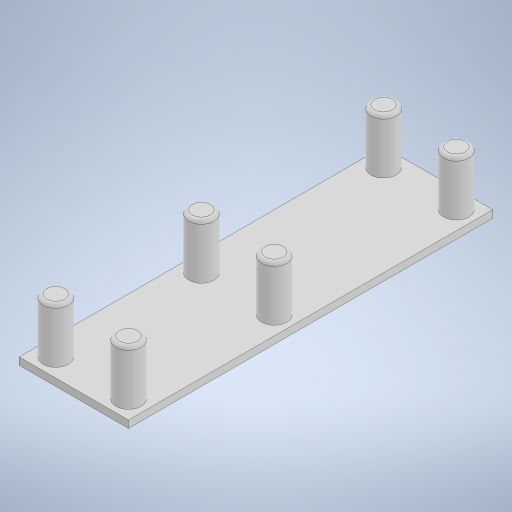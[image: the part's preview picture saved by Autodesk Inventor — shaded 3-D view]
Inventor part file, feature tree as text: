
AUTODESK INVENTOR PART (.ipt)
format: ipt  version: 2024.1 (Build 281209000, 209)  size: 441,344 bytes
history: native  units: in
note: dims shown in document units (in); Inventor stores cm internally (conversion verified against a paired STEP export)
features: extrude x4, sketch x4, fillet x2
ambient origin geometry x8: Origin, YZ Plane, XZ Plane, XY Plane, X Axis, Y Axis, Z Axis, Center Point
bodies: Solid1 (feature_tree)
feature tree (10):
  extrude  "Extrusion1"  Depth=1.1811in
  extrude  "Extrusion2"  Depth=0.0787in
  extrude  "Extrusion3"  Depth=1.5748in
  extrude  "Extrusion4"  Depth=1.969in
  fillet  "Fillet1"  Radius=1.969in
  fillet  "Fillet2"  Radius=0.3935in
  sketch  "Sketch1"  dims[d0=3.937in d1=1.1811in]
  sketch  "Sketch2"  dims[d2=0.0787in d3=0.0in d4=0.1969in]
  sketch  "Sketch3"  dims[d5=0.1969in d6=1.5748in]
  sketch  "Sketch4"  dims[d7=1.5748in d8=1.969in d9=1.969in d10=0.3935in d11=0.3935in d12=0.2756in d13=0.2756in d14=0.2756in d15=0.2756in d16=0.2756in d17=0.2756in d18=0.2362in d19=0.2362in d20=0.2362in d21=0.2362in d22=0.2362in d23=0.2362in d24=0.5512in d25=0.0in d26=0.5512in d27=0.0in d28=0.2756in d29=0.0394in d30=0.0in d31=0.0394in d32=0.0394in]
